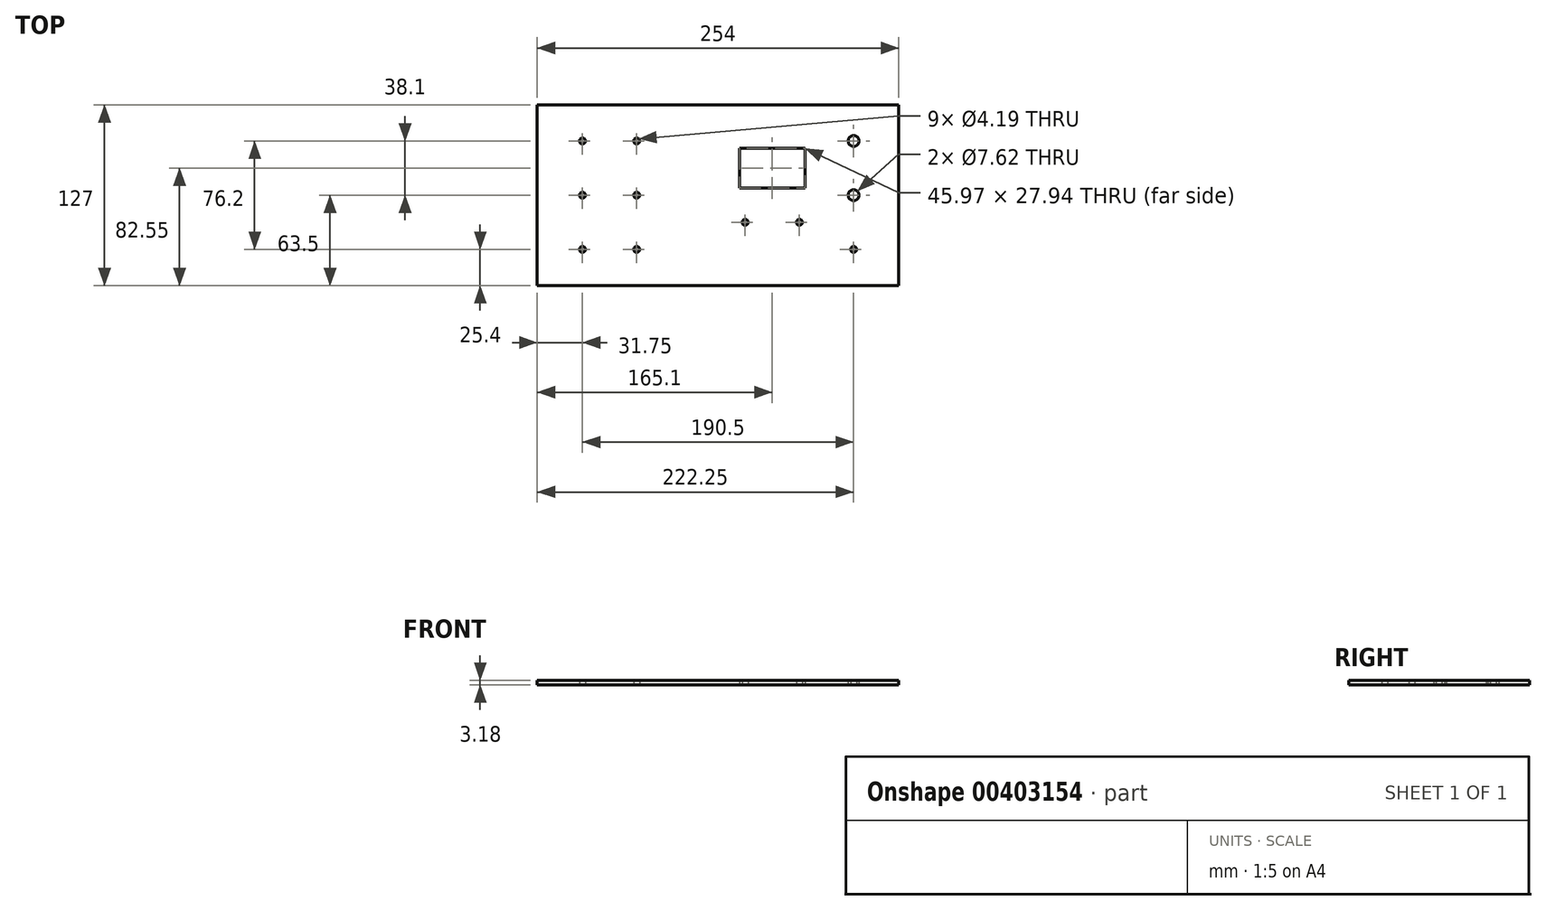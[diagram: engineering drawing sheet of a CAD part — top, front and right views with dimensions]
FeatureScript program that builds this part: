
annotation { "Feature Type Name" : "Feature", "Feature Type Description" : "" }
export const myFeature = defineFeature(function(context is Context, id is Id, definition is map)
    precondition{}
    {
        {
            var Q0;
            Q0=qCreatedBy(makeId("Top.planeOp"),FACE);
            var sketch = newSketch(context, id + "F0", { "sketchPlane" : qUnion([Q0])});
            skLineSegment(sketch, "E0.bottom", {"start": v(127, -63.5) * mm, "end": v(-127, -63.5) * mm});
            skLineSegment(sketch, "E0.top", {"start": v(127, 63.5) * mm, "end": v(-127, 63.5) * mm});
            skLineSegment(sketch, "E0.left", {"start": v(127, -63.5) * mm, "end": v(127, 63.5) * mm});
            skLineSegment(sketch, "E0.right", {"start": v(-127, -63.5) * mm, "end": v(-127, 63.5) * mm});
            skPoint(sketch, "E0.middle", {"position": v(0, 0) * mm});
            skLineSegment(sketch, "E1", {"start": v(0, 63.5) * mm, "end": v(0, -63.5) * mm});
            skLineSegment(sketch, "E2.bottom", {"start": v(19.05, -63.5) * mm, "end": v(-19.05, -63.5) * mm});
            skLineSegment(sketch, "E2.top", {"start": v(19.05, 63.5) * mm, "end": v(-19.05, 63.5) * mm});
            skLineSegment(sketch, "E2.left", {"start": v(19.05, -63.5) * mm, "end": v(19.05, 63.5) * mm});
            skLineSegment(sketch, "E2.right", {"start": v(-19.05, -63.5) * mm, "end": v(-19.05, 63.5) * mm});
            skLineSegment(sketch, "E3.bottom", {"start": v(57.15, -63.5) * mm, "end": v(-57.15, -63.5) * mm});
            skLineSegment(sketch, "E3.top", {"start": v(57.15, 63.5) * mm, "end": v(-57.15, 63.5) * mm});
            skLineSegment(sketch, "E3.left", {"start": v(57.15, -63.5) * mm, "end": v(57.15, 63.5) * mm});
            skLineSegment(sketch, "E3.right", {"start": v(-57.15, -63.5) * mm, "end": v(-57.15, 63.5) * mm});
            skLineSegment(sketch, "E4.bottom", {"start": v(95.25, -63.5) * mm, "end": v(-95.25, -63.5) * mm});
            skLineSegment(sketch, "E4.top", {"start": v(95.25, 63.5) * mm, "end": v(-95.25, 63.5) * mm});
            skLineSegment(sketch, "E4.left", {"start": v(95.25, -63.5) * mm, "end": v(95.25, 63.5) * mm});
            skLineSegment(sketch, "E4.right", {"start": v(-95.25, -63.5) * mm, "end": v(-95.25, 63.5) * mm});
            skLineSegment(sketch, "E5", {"start": v(-127, 0) * mm, "end": v(127, 0) * mm});
            skLineSegment(sketch, "E6.bottom", {"start": v(127, -38.1) * mm, "end": v(-127, -38.1) * mm});
            skLineSegment(sketch, "E6.top", {"start": v(127, 38.1) * mm, "end": v(-127, 38.1) * mm});
            skLineSegment(sketch, "E6.left", {"start": v(127, -38.1) * mm, "end": v(127, 38.1) * mm});
            skLineSegment(sketch, "E6.right", {"start": v(-127, -38.1) * mm, "end": v(-127, 38.1) * mm});
            skLineSegment(sketch, "E7.bottom", {"start": v(127, -19.05) * mm, "end": v(-127, -19.05) * mm});
            skLineSegment(sketch, "E7.top", {"start": v(127, 19.05) * mm, "end": v(-127, 19.05) * mm});
            skLineSegment(sketch, "E7.left", {"start": v(127, -19.05) * mm, "end": v(127, 19.05) * mm});
            skLineSegment(sketch, "E7.right", {"start": v(-127, -19.05) * mm, "end": v(-127, 19.05) * mm});
            skPoint(sketch, "E8", {"position": v(95.25, 38.1) * mm});
            skPoint(sketch, "E9", {"position": v(95.25, 19.05) * mm});
            skPoint(sketch, "E10", {"position": v(95.25, 0) * mm});
            skPoint(sketch, "E11", {"position": v(95.25, -19.05) * mm});
            skPoint(sketch, "E12", {"position": v(95.25, -38.1) * mm});
            skPoint(sketch, "E13", {"position": v(57.15, -38.1) * mm});
            skPoint(sketch, "E14", {"position": v(57.15, -19.05) * mm});
            skPoint(sketch, "E15", {"position": v(57.15, 0) * mm});
            skPoint(sketch, "E16", {"position": v(57.15, 19.05) * mm});
            skPoint(sketch, "E17", {"position": v(57.15, 38.1) * mm});
            skPoint(sketch, "E18", {"position": v(19.05, -38.1) * mm});
            skPoint(sketch, "E19", {"position": v(19.05, -19.05) * mm});
            skPoint(sketch, "E20", {"position": v(19.05, 0) * mm});
            skPoint(sketch, "E21", {"position": v(19.05, 19.05) * mm});
            skPoint(sketch, "E22", {"position": v(19.05, 38.1) * mm});
            skPoint(sketch, "E23", {"position": v(-19.05, -38.1) * mm});
            skPoint(sketch, "E24", {"position": v(-19.05, -19.05) * mm});
            skPoint(sketch, "E25", {"position": v(-19.05, 0) * mm});
            skPoint(sketch, "E26", {"position": v(-19.05, 19.05) * mm});
            skPoint(sketch, "E27", {"position": v(-19.05, 38.1) * mm});
            skPoint(sketch, "E28", {"position": v(-57.15, -38.1) * mm});
            skPoint(sketch, "E29", {"position": v(-57.15, -19.05) * mm});
            skPoint(sketch, "E30", {"position": v(-57.15, 0) * mm});
            skPoint(sketch, "E31", {"position": v(-57.15, 19.05) * mm});
            skPoint(sketch, "E32", {"position": v(-57.15, 38.1) * mm});
            skPoint(sketch, "E33", {"position": v(-95.25, -38.1) * mm});
            skPoint(sketch, "E34", {"position": v(-95.25, -19.05) * mm});
            skPoint(sketch, "E35", {"position": v(-95.25, 0) * mm});
            skPoint(sketch, "E36", {"position": v(-95.25, 19.05) * mm});
            skPoint(sketch, "E37", {"position": v(-95.25, 38.1) * mm});
            skPoint(sketch, "E38", {"position": v(38.1, 19.05) * mm});
            skSolve(sketch);
        }
        {
            var Q0;
            Q0=qCreatedBy(makeId("Top.planeOp"),FACE);
            var sketch = newSketch(context, id + "F1", { "sketchPlane" : qUnion([Q0])});
            skLineSegment(sketch, "E39.0", {"start": v(127, -63.5) * mm, "end": v(-127, -63.5) * mm});
            skLineSegment(sketch, "E40.0", {"start": v(-127, -63.5) * mm, "end": v(-127, 63.5) * mm});
            skLineSegment(sketch, "E41.0", {"start": v(127, -63.5) * mm, "end": v(127, 63.5) * mm});
            skLineSegment(sketch, "E42.0", {"start": v(127, 63.5) * mm, "end": v(-127, 63.5) * mm});
            skPoint(sketch, "E43.0", {"position": v(95.25, 38.1) * mm});
            skPoint(sketch, "E44.0", {"position": v(95.25, 0) * mm});
            skPoint(sketch, "E45.0", {"position": v(95.25, -38.1) * mm});
            skPoint(sketch, "E46.0", {"position": v(57.15, -19.05) * mm});
            skPoint(sketch, "E47.0", {"position": v(19.05, -19.05) * mm});
            skPoint(sketch, "E48.0", {"position": v(-57.15, -38.1) * mm});
            skPoint(sketch, "E49.0", {"position": v(-95.25, -38.1) * mm});
            skPoint(sketch, "E50.0", {"position": v(-95.25, 0) * mm});
            skPoint(sketch, "E51.0", {"position": v(-57.15, 0) * mm});
            skPoint(sketch, "E52.0", {"position": v(-57.15, 38.1) * mm});
            skPoint(sketch, "E53.0", {"position": v(-95.25, 38.1) * mm});
            skPoint(sketch, "E54.0", {"position": v(38.1, 19.05) * mm});
            skLineSegment(sketch, "E55.bottom", {"start": v(61.09, 5.08) * mm, "end": v(15.11, 5.08) * mm});
            skLineSegment(sketch, "E55.top", {"start": v(61.09, 33.02) * mm, "end": v(15.11, 33.02) * mm});
            skLineSegment(sketch, "E55.left", {"start": v(61.09, 5.08) * mm, "end": v(61.09, 33.02) * mm});
            skLineSegment(sketch, "E55.right", {"start": v(15.11, 5.08) * mm, "end": v(15.11, 33.02) * mm});
            skCircle(sketch, "E56", {"center": v(95.25, 38.1) * mm, "radius": 3.81 * mm});
            skCircle(sketch, "E57", {"center": v(95.25, 0) * mm, "radius": 3.81 * mm});
            skCircle(sketch, "E58", {"center": v(95.25, -38.1) * mm, "radius": 2.1 * mm});
            skCircle(sketch, "E59", {"center": v(57.15, -19.05) * mm, "radius": 2.1 * mm});
            skCircle(sketch, "E60", {"center": v(19.05, -19.05) * mm, "radius": 2.1 * mm});
            skCircle(sketch, "E61", {"center": v(-57.15, -38.1) * mm, "radius": 2.1 * mm});
            skCircle(sketch, "E62", {"center": v(-95.25, -38.1) * mm, "radius": 2.1 * mm});
            skCircle(sketch, "E63", {"center": v(-57.15, 0) * mm, "radius": 2.1 * mm});
            skCircle(sketch, "E64", {"center": v(-95.25, 0) * mm, "radius": 2.1 * mm});
            skCircle(sketch, "E65", {"center": v(-57.15, 38.1) * mm, "radius": 2.1 * mm});
            skCircle(sketch, "E66", {"center": v(-95.25, 38.1) * mm, "radius": 2.1 * mm});
            skSolve(sketch);
        }
        {
            var Q0;
            Q0=makeQuery(id+"F1.imprint","IMPRINT",FACE,{"disambiguationData":[TD([[makeQuery(id+"F1.imprint","IMPRINT",EDGE,{"derivedFrom":sQuery(id+"F1.wireOp",EDGE,"E39.0")}),-1.0]])]});
            extrude(context, id + "F2", {"entities" : qUnion([Q0]), "depth" : 3.17 * mm});
        }
    });
